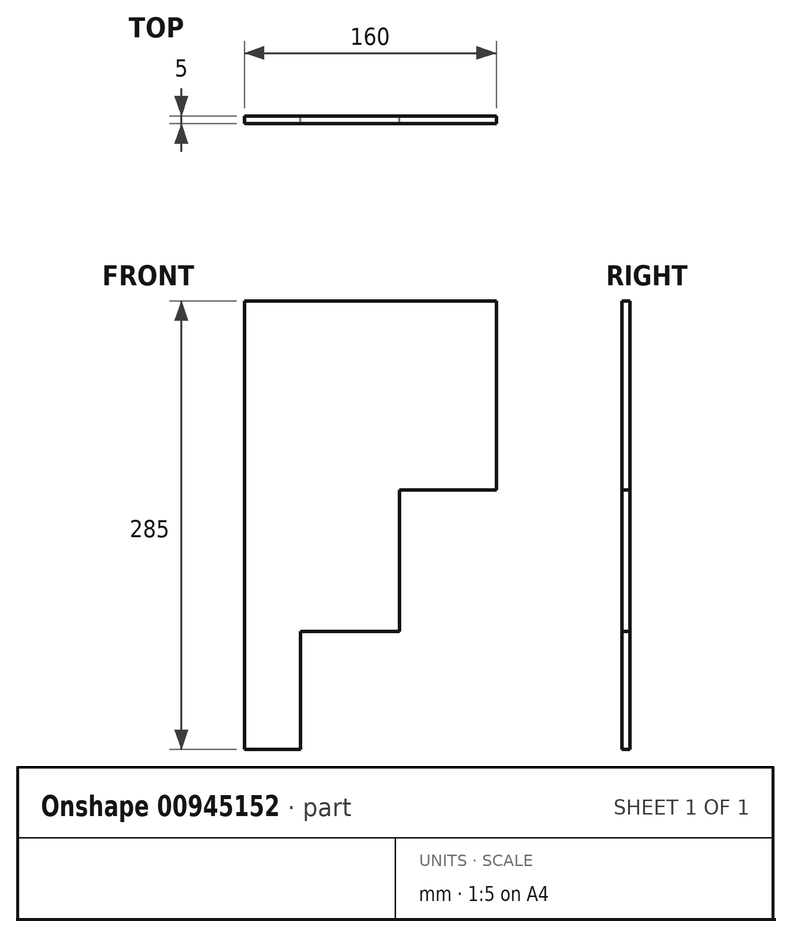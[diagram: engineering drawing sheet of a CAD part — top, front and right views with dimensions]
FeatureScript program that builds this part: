
annotation { "Feature Type Name" : "Feature", "Feature Type Description" : "" }
export const myFeature = defineFeature(function(context is Context, id is Id, definition is map)
    precondition{}
    {
        {
            var Q0;
            Q0=qCreatedBy(makeId("Front.planeOp"),FACE);
            var sketch = newSketch(context, id + "F0", { "sketchPlane" : qUnion([Q0])});
            skLineSegment(sketch, "E0", {"start": v(-118.96, 142.3) * mm, "end": v(-118.96, -142.7) * mm});
            skLineSegment(sketch, "E1", {"start": v(-118.96, -142.7) * mm, "end": v(-83.25, -142.7) * mm});
            skLineSegment(sketch, "E2", {"start": v(-83.25, -142.7) * mm, "end": v(-83.25, -67.7) * mm});
            skLineSegment(sketch, "E3", {"start": v(-83.25, -67.7) * mm, "end": v(-20.28, -67.7) * mm});
            skLineSegment(sketch, "E4", {"start": v(-20.28, -67.7) * mm, "end": v(-20.28, 22.3) * mm});
            skLineSegment(sketch, "E5", {"start": v(-20.28, 22.3) * mm, "end": v(41.04, 22.3) * mm});
            skLineSegment(sketch, "E6", {"start": v(41.04, 22.3) * mm, "end": v(41.04, 142.3) * mm});
            skLineSegment(sketch, "E7", {"start": v(41.04, 142.3) * mm, "end": v(-118.96, 142.3) * mm});
            skSolve(sketch);
        }
        {
            var Q0;
            Q0=makeQuery(id+"F0.imprint","IMPRINT",FACE,{"disambiguationData":[TD([[makeQuery(id+"F0.imprint","IMPRINT",EDGE,{"derivedFrom":sQuery(id+"F0.wireOp",EDGE,"E0")}),1.0]])]});
            extrude(context, id + "F1", {"entities" : qUnion([Q0]), "depth" : 5 * mm, "offsetDistance" : 25 * mm});
        }
    });
